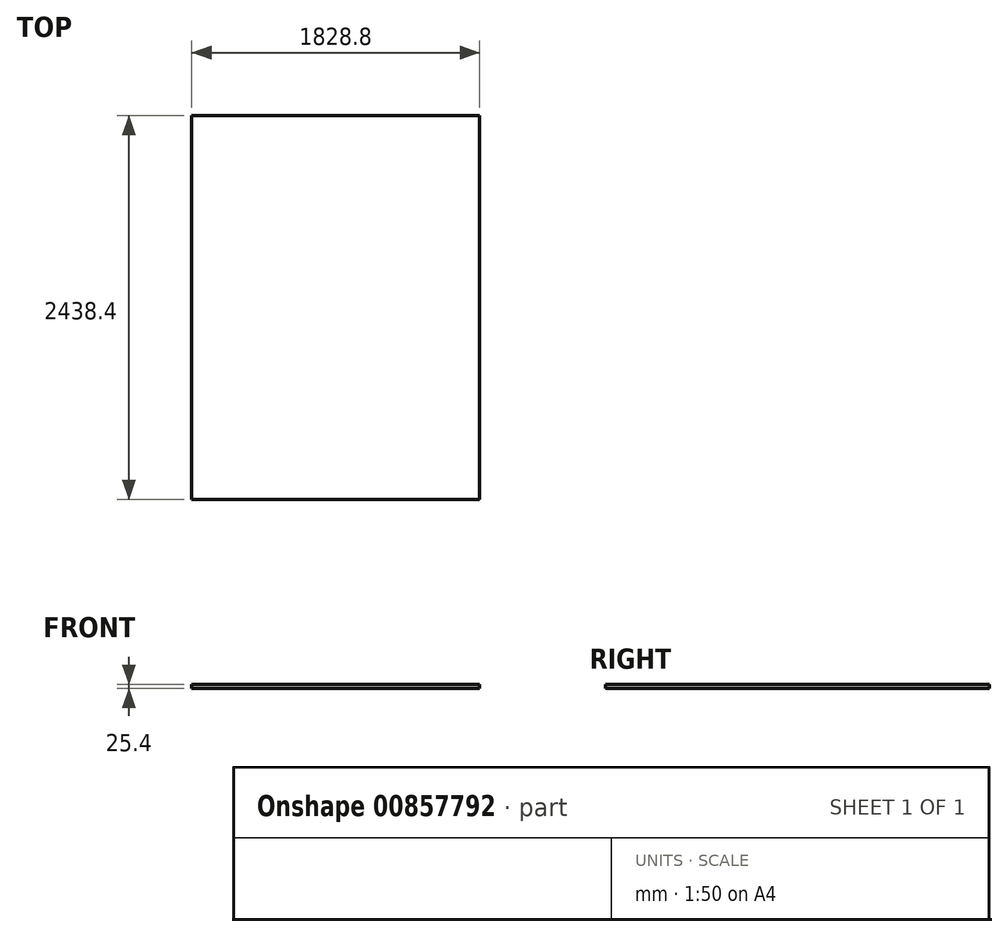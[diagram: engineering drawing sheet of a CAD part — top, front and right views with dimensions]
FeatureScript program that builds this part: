
annotation { "Feature Type Name" : "Feature", "Feature Type Description" : "" }
export const myFeature = defineFeature(function(context is Context, id is Id, definition is map)
    precondition{}
    {
        {
            var Q0;
            Q0=qCreatedBy(makeId("Top.planeOp"),FACE);
            var sketch = newSketch(context, id + "F0", { "sketchPlane" : qUnion([Q0])});
            skLineSegment(sketch, "E0.bottom", {"start": v(-914.4, 1219.2) * mm, "end": v(914.4, 1219.2) * mm});
            skLineSegment(sketch, "E0.top", {"start": v(-914.4, -1219.2) * mm, "end": v(914.4, -1219.2) * mm});
            skLineSegment(sketch, "E0.left", {"start": v(-914.4, 1219.2) * mm, "end": v(-914.4, -1219.2) * mm});
            skLineSegment(sketch, "E0.right", {"start": v(914.4, 1219.2) * mm, "end": v(914.4, -1219.2) * mm});
            skPoint(sketch, "E0.middle", {"position": v(0, 0) * mm});
            skSolve(sketch);
        }
        {
            var Q0;
            Q0=makeQuery(id+"F0.imprint","IMPRINT",FACE,{"disambiguationData":[TD([[makeQuery(id+"F0.imprint","IMPRINT",EDGE,{"derivedFrom":sQuery(id+"F0.wireOp",EDGE,"E0.bottom")}),-1.0]])]});
            extrude(context, id + "F1", {"entities" : qUnion([Q0]), "oppositeDirection" : true, "depth" : 25.4 * mm, "offsetDistance" : 25.4 * mm});
        }
    });
